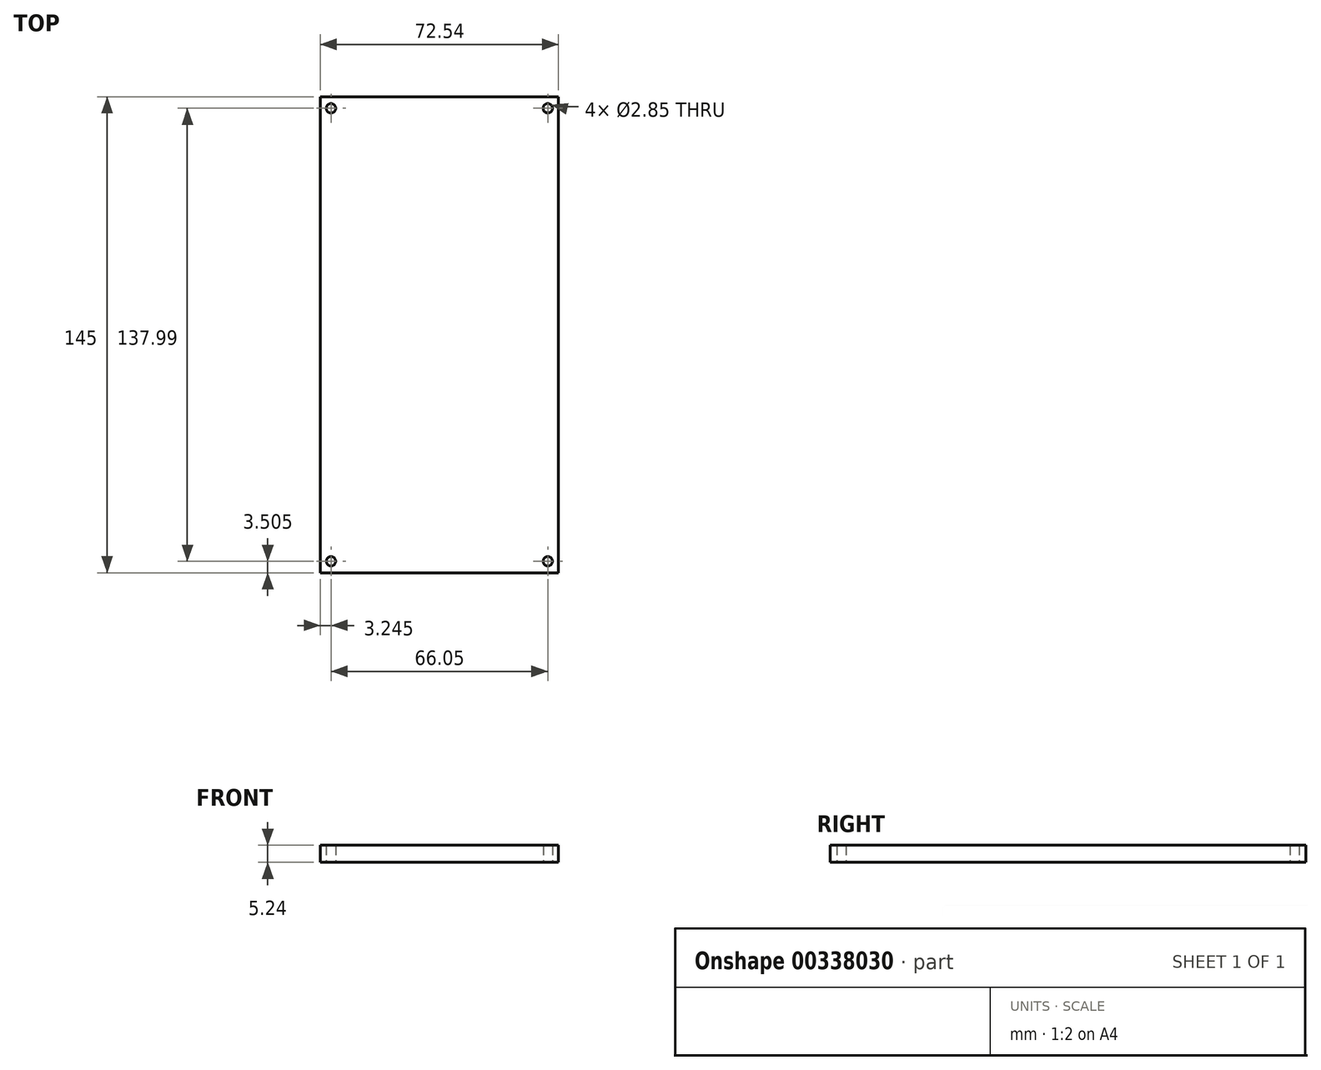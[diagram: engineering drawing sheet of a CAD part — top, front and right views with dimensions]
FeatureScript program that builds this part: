
annotation { "Feature Type Name" : "Feature", "Feature Type Description" : "" }
export const myFeature = defineFeature(function(context is Context, id is Id, definition is map)
    precondition{}
    {
        {
            var Q0;
            Q0=qCreatedBy(makeId("Top.planeOp"),FACE);
            var sketch = newSketch(context, id + "F0", { "sketchPlane" : qUnion([Q0])});
            skLineSegment(sketch, "E0.bottom", {"start": v(-36.27, -72.5) * mm, "end": v(-36.27, 72.5) * mm});
            skLineSegment(sketch, "E0.top", {"start": v(36.27, -72.5) * mm, "end": v(36.27, 72.5) * mm});
            skLineSegment(sketch, "E0.left", {"start": v(-36.27, -72.5) * mm, "end": v(36.27, -72.5) * mm});
            skLineSegment(sketch, "E0.right", {"start": v(-36.27, 72.5) * mm, "end": v(36.27, 72.5) * mm});
            skPoint(sketch, "E0.middle", {"position": v(0, 0) * mm});
            skPoint(sketch, "E1", {"position": v(0, 72.5) * mm});
            skPoint(sketch, "E2", {"position": v(36.27, 0) * mm});
            skCircle(sketch, "E3", {"center": v(33.03, 69) * mm, "radius": 1.43 * mm});
            skCircle(sketch, "E4", {"center": v(-33.03, 69) * mm, "radius": 1.43 * mm});
            skCircle(sketch, "E5", {"center": v(33.03, -69) * mm, "radius": 1.43 * mm});
            skCircle(sketch, "E6", {"center": v(-33.03, -69) * mm, "radius": 1.43 * mm});
            skSolve(sketch);
        }
        {
            var Q0;
            Q0=qSketchRegion(id+"F0",true);
            extrude(context, id + "F1", {"entities" : qUnion([Q0]), "depth" : 5.24 * mm, "offsetDistance" : 25 * mm});
        }
    });
